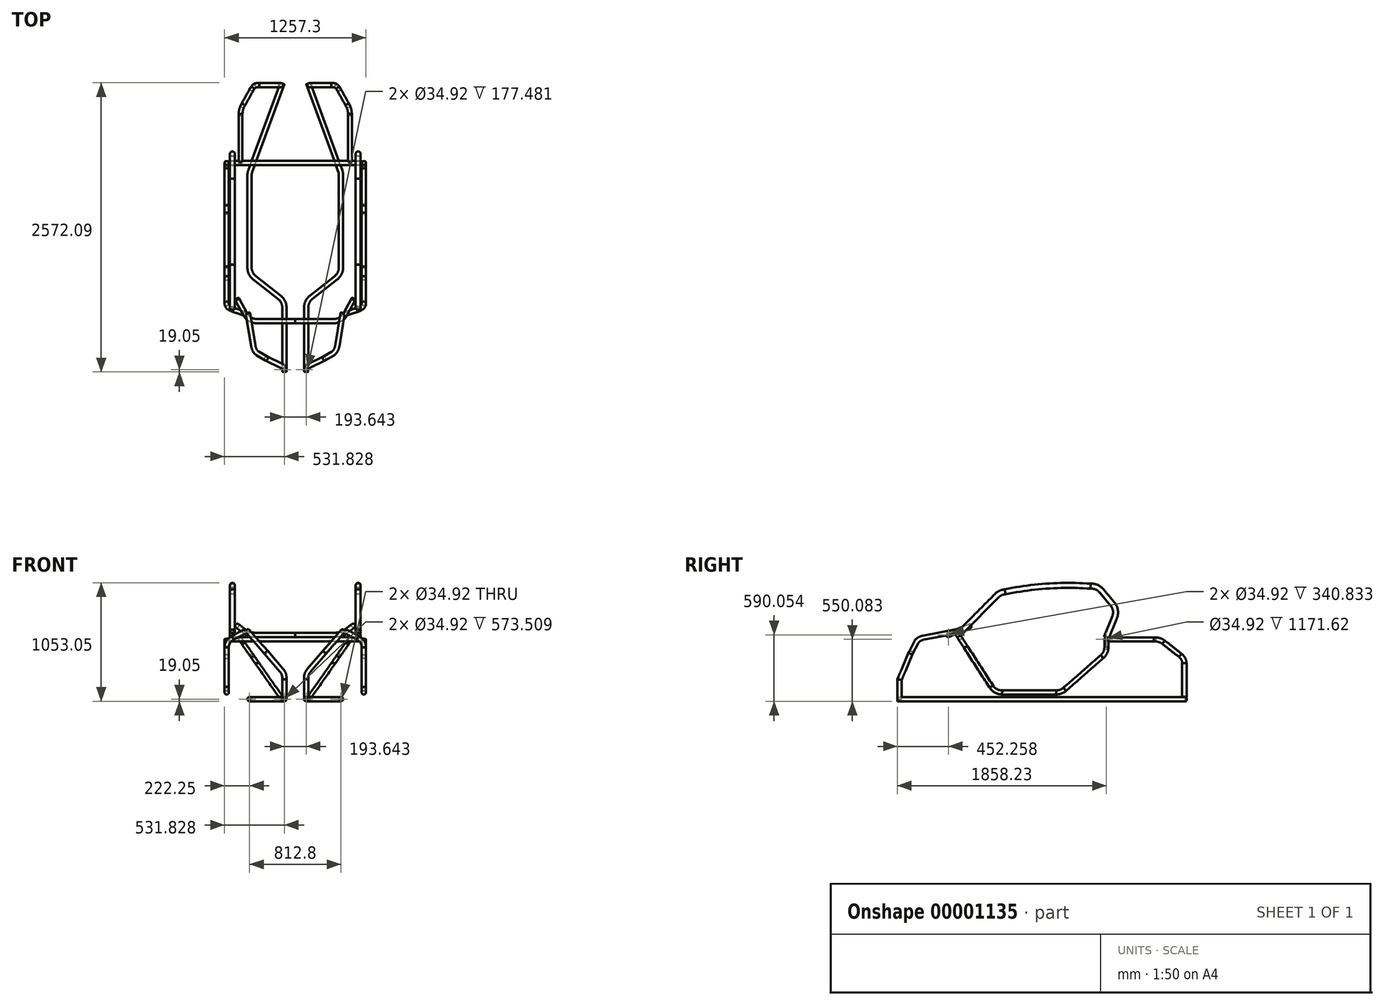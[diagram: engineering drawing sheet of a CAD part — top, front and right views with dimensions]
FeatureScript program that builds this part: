
annotation { "Feature Type Name" : "Feature", "Feature Type Description" : "" }
export const myFeature = defineFeature(function(context is Context, id is Id, definition is map)
    precondition{}
    {
        {
            var Q0;
            Q0=qCreatedBy(makeId("Right.planeOp"),FACE);
            cPlane(context, id + "F0", {"entities" : qUnion([Q0]), "cplaneType" : CPlaneType.OFFSET, "offset" : 609.6 * mm, "width" : 152.4 * mm, "height" : 152.4 * mm});
        }
        {
            var Q0;
            Q0=qCreatedBy(id+"F0.planeOp",FACE);
            var sketch = newSketch(context, id + "F1", { "sketchPlane" : qUnion([Q0])});
            skLineSegment(sketch, "E0", {"start": v(-375.35, 286.33) * mm, "end": v(-147.95, -65.95) * mm});
            skLineSegment(sketch, "E1", {"start": v(-51.92, -118.26) * mm, "end": v(429.24, -118.26) * mm});
            skLineSegment(sketch, "E2", {"start": v(504.5, -90) * mm, "end": v(836.46, 200.4) * mm});
            skPoint(sketch, "E3.visualSharp", {"position": v(-114.18, -118.26) * mm});
            skArc(sketch, "E3.filletArc", {"start": v(-147.95, -65.95) * mm, "mid": v(-106.6, -104.34) * mm, "end": v(-51.92, -118.26) * mm});
            skPoint(sketch, "E4.visualSharp", {"position": v(472.18, -118.26) * mm});
            skArc(sketch, "E4.filletArc", {"start": v(429.24, -118.26) * mm, "mid": v(469.44, -110.96) * mm, "end": v(504.5, -90) * mm});
            skPoint(sketch, "E5", {"position": v(188.66, 338.94) * mm});
            skPoint(sketch, "E5.positionSnap0", {"position": v(188.66, -118.26) * mm});
            skLineSegment(sketch, "E6", {"start": v(875.5, 286.43) * mm, "end": v(875.5, 353.23) * mm});
            skPoint(sketch, "E7.visualSharp", {"position": v(875.5, 234.56) * mm});
            skArc(sketch, "E7.filletArc", {"start": v(836.46, 200.4) * mm, "mid": v(865.3, 239.2) * mm, "end": v(875.5, 286.43) * mm});
            skSolve(sketch);
        }
        {
            var Q0;
            Q0=sQuery(id+"F1.wireOp",EDGE,"E0");
            cPlane(context, id + "F2", {"entities" : qUnion([Q0]), "cplaneType" : CPlaneType.LINE_ANGLE, "offset" : 25.4 * mm, "angle" : 90 * degree, "flipAlignment" : true, "width" : 152.4 * mm, "height" : 152.4 * mm});
        }
        {
            var Q0;
            Q0=qCreatedBy(id+"F2.planeOp",FACE);
            var sketch = newSketch(context, id + "F3", { "sketchPlane" : qUnion([Q0])});
            skPoint(sketch, "E8.0", {"position": v(-609.6, 444.13) * mm});
            skLineSegment(sketch, "E9", {"start": v(-609.6, 444.13) * mm, "end": v(-609.6, 444.13) * mm});
            skLineSegment(sketch, "E10", {"start": v(-555.72, 541.15) * mm, "end": v(-447.92, 608.3) * mm});
            skLineSegment(sketch, "E11", {"start": v(-446.58, 606.13) * mm, "end": v(-447.92, 608.3) * mm});
            skArc(sketch, "E12.filletArc", {"start": v(-555.72, 541.15) * mm, "mid": v(-595.23, 499.62) * mm, "end": v(-609.6, 444.13) * mm});
            skSolve(sketch);
        }
        {
            var Q0;
            Q0=sQuery(id+"F3.wireOp",EDGE,"E11");
            cPlane(context, id + "F4", {"entities" : qUnion([Q0]), "cplaneType" : CPlaneType.LINE_ANGLE, "offset" : 25.4 * mm, "angle" : 0 * degree, "width" : 152.4 * mm, "height" : 152.4 * mm});
        }
        {
            var Q0;
            Q0=qCreatedBy(id+"F4.planeOp",FACE);
            var sketch = newSketch(context, id + "F5", { "sketchPlane" : qUnion([Q0])});
            skPoint(sketch, "E13.0", {"position": v(-464.38, 607.56) * mm});
            skCircle(sketch, "E14", {"center": v(-464.38, 607.56) * mm, "radius": 19.05 * mm});
            skCircle(sketch, "E15.0", {"center": v(-464.38, 607.56) * mm, "radius": 17.46 * mm});
            skSolve(sketch);
        }
        {
            var Q0;
            Q0=makeQuery(id+"F5.imprint","IMPRINT",FACE,{"disambiguationData":[TD([[makeQuery(id+"F5.imprint","IMPRINT",EDGE,{"derivedFrom":sQuery(id+"F5.wireOp",EDGE,"E14")}),1.0]])]});
            var Q1;
            Q1=sQuery(id+"F3.wireOp",EDGE,"E10");
            var Q2;
            Q2=sQuery(id+"F3.wireOp",EDGE,"E12.filletArc");
            var Q3;
            Q3=sQuery(id+"F3.wireOp",EDGE,"E9");
            var Q4;
            Q4=sQuery(id+"F1.wireOp",EDGE,"E0");
            var Q5;
            Q5=sQuery(id+"F1.wireOp",EDGE,"E3.filletArc");
            var Q6;
            Q6=sQuery(id+"F1.wireOp",EDGE,"E1");
            var Q7;
            Q7=sQuery(id+"F1.wireOp",EDGE,"E4.filletArc");
            var Q8;
            Q8=sQuery(id+"F1.wireOp",EDGE,"E2");
            var Q9;
            Q9=sQuery(id+"F1.wireOp",EDGE,"E7.filletArc");
            var Q10;
            Q10=sQuery(id+"F1.wireOp",EDGE,"E6");
            sweep(context, id + "F6", {"profiles" : qUnion([Q0]), "path" : qUnion([Q1, Q2, Q3, Q4, Q5, Q6, Q7, Q8, Q9, Q10])});
        }
        {
            var Q0;
            Q0=makeQuery(id+"F6.opSweep","SWEPT_BODY",BODY,{"disambiguationData":[OSD([sQuery(id+"F1.wireOp",EDGE,"E2"),sQuery(id+"F5.wireOp",EDGE,"E14"),sQuery(id+"F5.wireOp",EDGE,"E15.0")])]});
            var Q1;
            Q1=qCreatedBy(makeId("Right.planeOp"),FACE);
            mirror(context, id + "F7", {"entities" : qUnion([Q0]), "mirrorPlane" : qUnion([Q1])});
        }
        {
            var Q0;
            Q0=qCreatedBy(makeId("Right.planeOp"),FACE);
            var sketch = newSketch(context, id + "F8", { "sketchPlane" : qUnion([Q0])});
            skPoint(sketch, "E16.0", {"position": v(875.5, 353.23) * mm});
            skCircle(sketch, "E17", {"center": v(875.5, 353.23) * mm, "radius": 19.05 * mm});
            skCircle(sketch, "E18.0", {"center": v(875.5, 353.23) * mm, "radius": 17.46 * mm});
            skSolve(sketch);
        }
        {
            var Q0;
            Q0 = qSketchRegion(id + "F8", true);
            extrude(context, id + "F9", {"entities" : qUnion([Q0]), "endBound" : BoundingType.SYMMETRIC, "depth" : 1171.62 * mm, "offsetDistance" : 25.4 * mm});
        }
        {
            var Q0;
            Q0=qCreatedBy(makeId("Top.planeOp"),FACE);
            cPlane(context, id + "F10", {"entities" : qUnion([Q0]), "cplaneType" : CPlaneType.OFFSET, "offset" : 177.8 * mm, "oppositeDirection" : true, "width" : 152.4 * mm, "height" : 152.4 * mm});
        }
        {
            var Q0;
            Q0=qCreatedBy(id+"F10.planeOp",FACE);
            var sketch = newSketch(context, id + "F11", { "sketchPlane" : qUnion([Q0])});
            skLineSegment(sketch, "E19", {"start": v(114.3, 1582.8) * mm, "end": v(399.39, 806.72) * mm});
            skLineSegment(sketch, "E20", {"start": v(406.4, 767.31) * mm, "end": v(406.4, -54.1) * mm});
            skLineSegment(sketch, "E21", {"start": v(362.9, -143.82) * mm, "end": v(140.31, -319.49) * mm});
            skLineSegment(sketch, "E22", {"start": v(96.82, -409.21) * mm, "end": v(96.82, -982.72) * mm});
            skPoint(sketch, "E23.visualSharp", {"position": v(96.82, -353.8) * mm});
            skArc(sketch, "E23.filletArc", {"start": v(140.31, -319.49) * mm, "mid": v(108.27, -359.36) * mm, "end": v(96.82, -409.21) * mm});
            skPoint(sketch, "E24.visualSharp", {"position": v(406.4, -109.5) * mm});
            skArc(sketch, "E24.filletArc", {"start": v(362.9, -143.82) * mm, "mid": v(394.95, -103.95) * mm, "end": v(406.4, -54.1) * mm});
            skPoint(sketch, "E25.visualSharp", {"position": v(406.4, 787.64) * mm});
            skArc(sketch, "E25.filletArc", {"start": v(406.4, 767.31) * mm, "mid": v(404.63, 787.33) * mm, "end": v(399.39, 806.72) * mm});
            skLineSegment(sketch, "E26", {"start": v(96.82, -982.72) * mm, "end": v(135.98, -982.72) * mm});
            skLineSegment(sketch, "E27", {"start": v(114.3, 1582.8) * mm, "end": v(114.3, 1492.8) * mm, "construction": true});
            skSolve(sketch);
        }
        {
            var Q0;
            Q0=sQuery(id+"F11.wireOp",EDGE,"E26");
            cPlane(context, id + "F12", {"entities" : qUnion([Q0]), "cplaneType" : CPlaneType.LINE_ANGLE, "offset" : 25.4 * mm, "angle" : 0 * degree, "width" : 152.4 * mm, "height" : 152.4 * mm});
        }
        {
            var Q0;
            Q0=qCreatedBy(id+"F12.planeOp",FACE);
            var sketch = newSketch(context, id + "F13", { "sketchPlane" : qUnion([Q0])});
            skPoint(sketch, "E28.0", {"position": v(-96.82, -177.8) * mm});
            skCircle(sketch, "E29", {"center": v(-96.82, -177.8) * mm, "radius": 19.05 * mm});
            skCircle(sketch, "E30.0", {"center": v(-96.82, -177.8) * mm, "radius": 17.46 * mm});
            skSolve(sketch);
        }
        {
            var Q0;
            Q0=makeQuery(id+"F13.imprint","IMPRINT",FACE,{"disambiguationData":[TD([[makeQuery(id+"F13.imprint","IMPRINT",EDGE,{"derivedFrom":sQuery(id+"F13.wireOp",EDGE,"E29")}),1.0]])]});
            var Q1;
            Q1=sQuery(id+"F11.wireOp",EDGE,"E22");
            var Q2;
            Q2=sQuery(id+"F11.wireOp",EDGE,"E23.filletArc");
            var Q3;
            Q3=sQuery(id+"F11.wireOp",EDGE,"E21");
            var Q4;
            Q4=sQuery(id+"F11.wireOp",EDGE,"E24.filletArc");
            var Q5;
            Q5=sQuery(id+"F11.wireOp",EDGE,"E20");
            var Q6;
            Q6=sQuery(id+"F11.wireOp",EDGE,"E25.filletArc");
            var Q7;
            Q7=sQuery(id+"F11.wireOp",EDGE,"E19");
            sweep(context, id + "F14", {"profiles" : qUnion([Q0]), "path" : qUnion([Q1, Q2, Q3, Q4, Q5, Q6, Q7])});
        }
        {
            var Q0;
            Q0=makeQuery(id+"F14.opSweep","SWEPT_BODY",BODY,{"disambiguationData":[OSD([sQuery(id+"F11.wireOp",EDGE,"E19"),sQuery(id+"F13.wireOp",EDGE,"E29"),sQuery(id+"F13.wireOp",EDGE,"E30.0")])]});
            var Q1;
            Q1=qCreatedBy(makeId("Right.planeOp"),FACE);
            mirror(context, id + "F15", {"entities" : qUnion([Q0]), "mirrorPlane" : qUnion([Q1])});
        }
        {
            var Q0;
            Q0=sQuery(id+"F11.wireOp",EDGE,"E27");
            cPlane(context, id + "F16", {"entities" : qUnion([Q0]), "cplaneType" : CPlaneType.LINE_ANGLE, "offset" : 25.4 * mm, "angle" : 55 * degree, "width" : 152.4 * mm, "height" : 152.4 * mm});
        }
        {
            var Q0;
            Q0=qCreatedBy(id+"F16.planeOp",FACE);
            var sketch = newSketch(context, id + "F17", { "sketchPlane" : qUnion([Q0])});
            skLineSegment(sketch, "E31", {"start": v(1568.24, -56.08) * mm, "end": v(1568.24, 311.12) * mm});
            skLineSegment(sketch, "E32", {"start": v(1533.15, 393.52) * mm, "end": v(1384.63, 536.29) * mm});
            skLineSegment(sketch, "E33", {"start": v(1305.42, 568.19) * mm, "end": v(875.5, 568.19) * mm});
            skPoint(sketch, "E34.visualSharp", {"position": v(1568.24, 359.8) * mm});
            skArc(sketch, "E34.filletArc", {"start": v(1568.24, 311.12) * mm, "mid": v(1559.1, 355.9) * mm, "end": v(1533.15, 393.52) * mm});
            skPoint(sketch, "E35.visualSharp", {"position": v(1351.45, 568.19) * mm});
            skArc(sketch, "E35.filletArc", {"start": v(1384.63, 536.29) * mm, "mid": v(1348.12, 559.91) * mm, "end": v(1305.42, 568.19) * mm});
            skPoint(sketch, "E36.0", {"position": v(1582.8, -80.09) * mm});
            skLineSegment(sketch, "E37", {"start": v(1568.24, -56.08) * mm, "end": v(1557.55, -56.08) * mm});
            skEllipse(sketch, "E38.0", {"center": v(875.5, 568.19) * mm, "majorRadius": 19.05 * mm, "minorRadius": 15.6 * mm, "majorAxis": v(1, 0), "construction": true});
            skEllipse(sketch, "E39", {"center": v(875.5, 568.19) * mm, "majorRadius": 21.32 * mm, "minorRadius": 17.46 * mm, "majorAxis": v(0, -1), "construction": true});
            skSolve(sketch);
        }
        {
            var Q0;
            Q0=sQuery(id+"F17.wireOp",EDGE,"E37");
            cPlane(context, id + "F18", {"entities" : qUnion([Q0]), "cplaneType" : CPlaneType.LINE_ANGLE, "offset" : 25.4 * mm, "angle" : 0 * degree, "width" : 152.4 * mm, "height" : 152.4 * mm});
        }
        {
            var Q0;
            Q0=qCreatedBy(id+"F18.planeOp",FACE);
            var sketch = newSketch(context, id + "F19", { "sketchPlane" : qUnion([Q0])});
            skPoint(sketch, "E40.0", {"position": v(128.07, -1568.24) * mm});
            skCircle(sketch, "E41", {"center": v(128.07, -1568.24) * mm, "radius": 19.05 * mm});
            skCircle(sketch, "E42.0", {"center": v(128.07, -1568.24) * mm, "radius": 17.46 * mm});
            skSolve(sketch);
        }
        {
            var Q0;
            Q0=makeQuery(id+"F19.imprint","IMPRINT",FACE,{"disambiguationData":[TD([[makeQuery(id+"F19.imprint","IMPRINT",EDGE,{"derivedFrom":sQuery(id+"F19.wireOp",EDGE,"E41")}),1.0]])]});
            var Q1;
            Q1=sQuery(id+"F17.wireOp",EDGE,"E31");
            var Q2;
            Q2=sQuery(id+"F17.wireOp",EDGE,"E34.filletArc");
            var Q3;
            Q3=sQuery(id+"F17.wireOp",EDGE,"E32");
            var Q4;
            Q4=sQuery(id+"F17.wireOp",EDGE,"E35.filletArc");
            var Q5;
            Q5=sQuery(id+"F17.wireOp",EDGE,"E33");
            sweep(context, id + "F20", {"profiles" : qUnion([Q0]), "path" : qUnion([Q1, Q2, Q3, Q4, Q5])});
        }
        {
            var Q0;
            Q0=makeQuery(id+"F20.opSweep","SWEPT_BODY",BODY,{"disambiguationData":[OSD([sQuery(id+"F17.wireOp",EDGE,"E33"),sQuery(id+"F19.wireOp",EDGE,"E41"),sQuery(id+"F19.wireOp",EDGE,"E42.0")])]});
            var Q1;
            Q1=qCreatedBy(makeId("Right.planeOp"),FACE);
            mirror(context, id + "F21", {"operationType" : NewBodyOperationType.ADD, "entities" : qUnion([Q0]), "mirrorPlane" : qUnion([Q1])});
        }
        {
            var Q0;
            Q0=qCreatedBy(makeId("Right.planeOp"),FACE);
            var sketch = newSketch(context, id + "F22", { "sketchPlane" : qUnion([Q0])});
            skPoint(sketch, "E43.0", {"position": v(-982.72, -177.8) * mm});
            skLineSegment(sketch, "E44", {"start": v(-982.72, -177.8) * mm, "end": v(-982.72, 0) * mm});
            skLineSegment(sketch, "E45", {"start": v(-982.72, 0) * mm, "end": v(-874.22, 257.34) * mm});
            skLineSegment(sketch, "E46", {"start": v(-874.22, 257.34) * mm, "end": v(-549.51, 393.2) * mm});
            skCircle(sketch, "E47", {"center": v(-530.46, 393.2) * mm, "radius": 19.05 * mm});
            skCircle(sketch, "E48.0", {"center": v(-530.46, 393.2) * mm, "radius": 17.46 * mm});
            skLineSegment(sketch, "E49", {"start": v(-574.37, 395.49) * mm, "end": v(-487.8, 431.7) * mm, "construction": true});
            skEllipse(sketch, "E50.0", {"center": v(-464.38, 424.25) * mm, "majorRadius": 19.05 * mm, "minorRadius": 15.3 * mm, "majorAxis": v(-1, 0)});
            skSolve(sketch);
        }
        {
            var Q0;
            Q0=qCreatedBy(makeId("Right.planeOp"),FACE);
            var sketch = newSketch(context, id + "F23", { "sketchPlane" : qUnion([Q0])});
            skPoint(sketch, "E51.0", {"position": v(-530.46, 393.2) * mm});
            skPoint(sketch, "E51.1", {"position": v(-464.38, 424.25) * mm});
            skLineSegment(sketch, "E52", {"start": v(-530.46, 393.2) * mm, "end": v(-464.38, 424.25) * mm});
            skLineSegment(sketch, "E53", {"start": v(-464.38, 424.25) * mm, "end": v(-289.04, 571.8) * mm});
            skSolve(sketch);
        }
        {
            var Q0;
            Q0=sQuery(id+"F22.wireOp",EDGE,"E46");
            cPlane(context, id + "F24", {"entities" : qUnion([Q0]), "cplaneType" : CPlaneType.LINE_ANGLE, "offset" : 25.4 * mm, "angle" : 0 * degree, "width" : 152.4 * mm, "height" : 152.4 * mm});
        }
        {
            var Q0;
            Q0=qCreatedBy(id+"F24.planeOp",FACE);
            var sketch = newSketch(context, id + "F25", { "sketchPlane" : qUnion([Q0])});
            skPoint(sketch, "E54.0", {"position": v(0, -337.58) * mm});
            skPoint(sketch, "E55.0", {"position": v(447.92, -264.64) * mm});
            skLineSegment(sketch, "E56", {"start": v(0, -337.58) * mm, "end": v(340.83, -337.58) * mm});
            skLineSegment(sketch, "E57", {"start": v(443.17, -274.19) * mm, "end": v(517.08, -125.62) * mm});
            skPoint(sketch, "E58.visualSharp", {"position": v(411.64, -337.58) * mm});
            skArc(sketch, "E58.filletArc", {"start": v(340.83, -337.58) * mm, "mid": v(401.02, -320.45) * mm, "end": v(443.17, -274.19) * mm});
            skSolve(sketch);
        }
        {
            var Q0;
            Q0=makeQuery(id+"F22.imprint","IMPRINT",FACE,{"disambiguationData":[TD([[makeQuery(id+"F22.imprint","IMPRINT",EDGE,{"derivedFrom":sQuery(id+"F22.wireOp",EDGE,"E47")}),1.0]])]});
            var Q1;
            Q1=sQuery(id+"F25.wireOp",EDGE,"E56");
            var Q2;
            Q2=sQuery(id+"F25.wireOp",EDGE,"E58.filletArc");
            var Q3;
            Q3=sQuery(id+"F25.wireOp",EDGE,"E57");
            sweep(context, id + "F26", {"profiles" : qUnion([Q0]), "path" : qUnion([Q1, Q2, Q3])});
        }
        {
            var Q0;
            Q0=makeQuery(id+"F26.opSweep","SWEPT_BODY",BODY,{"disambiguationData":[OSD([sQuery(id+"F22.wireOp",EDGE,"E47"),sQuery(id+"F22.wireOp",EDGE,"E48.0"),sQuery(id+"F25.wireOp",EDGE,"E57")])]});
            var Q1;
            Q1=qCreatedBy(makeId("Right.planeOp"),FACE);
            mirror(context, id + "F27", {"entities" : qUnion([Q0]), "mirrorPlane" : qUnion([Q1])});
        }
        {
            var Q0;
            Q0=qCreatedBy(makeId("Right.planeOp"),FACE);
            cPlane(context, id + "F28", {"entities" : qUnion([Q0]), "cplaneType" : CPlaneType.OFFSET, "offset" : 558.8 * mm, "width" : 152.4 * mm, "height" : 152.4 * mm});
        }
        {
            var Q0;
            Q0=qCreatedBy(id+"F28.planeOp",FACE);
            var sketch = newSketch(context, id + "F29", { "sketchPlane" : qUnion([Q0])});
            skCircle(sketch, "E59.0", {"center": v(875.5, 353.23) * mm, "radius": 19.05 * mm});
            skLineSegment(sketch, "E60", {"start": v(875.5, 372.28) * mm, "end": v(948, 551.55) * mm});
            skLineSegment(sketch, "E61", {"start": v(929.7, 667.75) * mm, "end": v(830.73, 786.03) * mm});
            skLineSegment(sketch, "E62", {"start": v(735.5, 826.73) * mm, "end": v(-25.2, 776.28) * mm, "construction": true});
            skLineSegment(sketch, "E63", {"start": v(-98.71, 742.8) * mm, "end": v(-414.93, 424.6) * mm});
            skPoint(sketch, "E64.visualSharp", {"position": v(973.72, 615.14) * mm});
            skArc(sketch, "E64.filletArc", {"start": v(948, 551.55) * mm, "mid": v(954.95, 612.19) * mm, "end": v(929.7, 667.75) * mm});
            skPoint(sketch, "E65.visualSharp", {"position": v(793.46, 830.58) * mm});
            skArc(sketch, "E65.filletArc", {"start": v(830.73, 786.03) * mm, "mid": v(788, 817.79) * mm, "end": v(735.5, 826.73) * mm});
            skPoint(sketch, "E66.visualSharp", {"position": v(-68.28, 773.42) * mm});
            skArc(sketch, "E66.filletArc", {"start": v(-25.2, 776.28) * mm, "mid": v(-65.02, 766.25) * mm, "end": v(-98.71, 742.8) * mm});
            skLineSegment(sketch, "E67", {"start": v(-414.93, 424.6) * mm, "end": v(-408.84, 418.55) * mm});
            skArc(sketch, "E68", {"start": v(735.5, 826.73) * mm, "mid": v(353.4, 827.93) * mm, "end": v(-25.2, 776.28) * mm});
            skSolve(sketch);
        }
        {
            var Q0;
            Q0=sQuery(id+"F29.wireOp",EDGE,"E67");
            cPlane(context, id + "F30", {"entities" : qUnion([Q0]), "cplaneType" : CPlaneType.LINE_ANGLE, "offset" : 25.4 * mm, "angle" : 0 * degree, "width" : 152.4 * mm, "height" : 152.4 * mm});
        }
        {
            var Q0;
            Q0=qCreatedBy(id+"F30.planeOp",FACE);
            var sketch = newSketch(context, id + "F31", { "sketchPlane" : qUnion([Q0])});
            skPoint(sketch, "E69.0", {"position": v(-558.8, 593.62) * mm});
            skCircle(sketch, "E70", {"center": v(-558.8, 593.62) * mm, "radius": 22.23 * mm});
            skCircle(sketch, "E71.0", {"center": v(-558.8, 593.62) * mm, "radius": 19.05 * mm});
            skSolve(sketch);
        }
        {
            var Q0;
            Q0=makeQuery(id+"F31.imprint","IMPRINT",FACE,{"disambiguationData":[TD([[makeQuery(id+"F31.imprint","IMPRINT",EDGE,{"derivedFrom":sQuery(id+"F31.wireOp",EDGE,"E70")}),1.0]])]});
            var Q1;
            Q1=sQuery(id+"F29.wireOp",EDGE,"E63");
            var Q2;
            Q2=sQuery(id+"F29.wireOp",EDGE,"E66.filletArc");
            var Q3;
            Q3=sQuery(id+"F29.wireOp",EDGE,"E65.filletArc");
            var Q4;
            Q4=sQuery(id+"F29.wireOp",EDGE,"E61");
            var Q5;
            Q5=sQuery(id+"F29.wireOp",EDGE,"E64.filletArc");
            var Q6;
            Q6=sQuery(id+"F29.wireOp",EDGE,"E60");
            var Q7;
            Q7=sQuery(id+"F29.wireOp",EDGE,"E68");
            sweep(context, id + "F32", {"profiles" : qUnion([Q0]), "path" : qUnion([Q1, Q2, Q3, Q4, Q5, Q6, Q7])});
        }
        {
            var Q0;
            Q0=makeQuery(id+"F32.opSweep","SWEPT_BODY",BODY,{"disambiguationData":[OSD([sQuery(id+"F29.wireOp",EDGE,"E60"),sQuery(id+"F31.wireOp",EDGE,"E70"),sQuery(id+"F31.wireOp",EDGE,"E71.0")])]});
            var Q1;
            Q1=qCreatedBy(makeId("Right.planeOp"),FACE);
            mirror(context, id + "F33", {"operationType" : NewBodyOperationType.ADD, "entities" : qUnion([Q0]), "mirrorPlane" : qUnion([Q1])});
        }
        {
            var Q0;
            Q0=qCreatedBy(id+"F10.planeOp",FACE);
            var sketch = newSketch(context, id + "F34", { "sketchPlane" : qUnion([Q0])});
            skCircle(sketch, "E72", {"center": v(96.82, -963.67) * mm, "radius": 19.05 * mm});
            skLineSegment(sketch, "E73.0", {"start": v(96.82, -409.21) * mm, "end": v(96.82, -982.72) * mm, "construction": true});
            skCircle(sketch, "E74.0", {"center": v(96.82, -963.67) * mm, "radius": 17.46 * mm});
            skSolve(sketch);
        }
        {
            var Q0;
            Q0=sQuery(id+"F22.wireOp",EDGE,"E45");
            cPlane(context, id + "F35", {"entities" : qUnion([Q0]), "cplaneType" : CPlaneType.LINE_ANGLE, "offset" : 25.4 * mm, "angle" : 90 * degree, "width" : 152.4 * mm, "height" : 152.4 * mm});
        }
        {
            var Q0;
            Q0=qCreatedBy(id+"F12.planeOp",FACE);
            var sketch = newSketch(context, id + "F36", { "sketchPlane" : qUnion([Q0])});
            skPoint(sketch, "E75.0", {"position": v(-96.82, -177.8) * mm});
            skLineSegment(sketch, "E76", {"start": v(-96.82, -177.8) * mm, "end": v(-96.82, 0) * mm});
            skSolve(sketch);
        }
        {
            var Q0;
            Q0=qCreatedBy(id+"F35.planeOp",FACE);
            var sketch = newSketch(context, id + "F37", { "sketchPlane" : qUnion([Q0])});
            skPoint(sketch, "E77.0", {"position": v(-96.82, -381.79) * mm});
            skLineSegment(sketch, "E78", {"start": v(-96.82, -381.79) * mm, "end": v(-96.82, -359.25) * mm});
            skLineSegment(sketch, "E79", {"start": v(-121.86, -287.86) * mm, "end": v(-258.4, -117.13) * mm});
            skPoint(sketch, "E80.visualSharp", {"position": v(-96.82, -319.16) * mm});
            skArc(sketch, "E80.filletArc", {"start": v(-96.82, -359.25) * mm, "mid": v(-103.26, -321.42) * mm, "end": v(-121.86, -287.86) * mm});
            skSolve(sketch);
        }
        {
            var Q0;
            Q0=sQuery(id+"F37.wireOp",EDGE,"E79");
            cPlane(context, id + "F38", {"entities" : qUnion([Q0]), "cplaneType" : CPlaneType.LINE_ANGLE, "offset" : 25.4 * mm, "angle" : 0 * degree, "width" : 152.4 * mm, "height" : 152.4 * mm});
        }
        {
            var Q0;
            Q0=qCreatedBy(id+"F38.planeOp",FACE);
            var sketch = newSketch(context, id + "F39", { "sketchPlane" : qUnion([Q0])});
            skPoint(sketch, "E81.0", {"position": v(-879.9, 353.55) * mm});
            skPoint(sketch, "E82.0", {"position": v(-464.38, 614) * mm});
            skLineSegment(sketch, "E83", {"start": v(-879.9, 353.55) * mm, "end": v(-834.4, 471.14) * mm});
            skLineSegment(sketch, "E84", {"start": v(-755.68, 540.75) * mm, "end": v(-464.38, 614) * mm});
            skPoint(sketch, "E85.visualSharp", {"position": v(-813.06, 526.32) * mm});
            skArc(sketch, "E85.filletArc", {"start": v(-755.68, 540.75) * mm, "mid": v(-803.52, 515.53) * mm, "end": v(-834.4, 471.14) * mm});
            skSolve(sketch);
        }
        {
            var Q0;
            Q0=makeQuery(id+"F34.imprint","IMPRINT",FACE,{"disambiguationData":[TD([[makeQuery(id+"F34.imprint","IMPRINT",EDGE,{"derivedFrom":sQuery(id+"F34.wireOp",EDGE,"E72")}),1.0]])]});
            var Q1;
            Q1=sQuery(id+"F36.wireOp",EDGE,"E76");
            var Q2;
            Q2=sQuery(id+"F37.wireOp",EDGE,"E78");
            var Q3;
            Q3=sQuery(id+"F37.wireOp",EDGE,"E80.filletArc");
            var Q4;
            Q4=sQuery(id+"F37.wireOp",EDGE,"E79");
            var Q5;
            Q5=sQuery(id+"F39.wireOp",EDGE,"E83");
            var Q6;
            Q6=sQuery(id+"F39.wireOp",EDGE,"E85.filletArc");
            var Q7;
            Q7=sQuery(id+"F39.wireOp",EDGE,"E84");
            sweep(context, id + "F40", {"profiles" : qUnion([Q0]), "path" : qUnion([Q1, Q2, Q3, Q4, Q5, Q6, Q7])});
        }
        {
            var Q0;
            Q0=makeQuery(id+"F40.opSweep","SWEPT_BODY",BODY,{"disambiguationData":[OSD([sQuery(id+"F34.wireOp",EDGE,"E72"),sQuery(id+"F34.wireOp",EDGE,"E74.0"),sQuery(id+"F39.wireOp",EDGE,"E84")])]});
            var Q1;
            Q1=qCreatedBy(makeId("Right.planeOp"),FACE);
            mirror(context, id + "F41", {"entities" : qUnion([Q0]), "mirrorPlane" : qUnion([Q1])});
        }
    });
